# Revit family: Loudspeaker-Ceiling Mounted-Q-SYS-AD-C6T-High Ceiling
name_source: partatom
category: Communication Devices
units: mm (PartAtom-declared; Revit-internal decimal feet)

## family parameters
Cut with Voids When Loaded = No
Host = Face
Maintain Annotation Orientation = No
OmniClass Number = 23.85.10.11.14.14.14
OmniClass Title = Loudspeakers
Part Type = Normal
Room Calculation Point = No
Round Connector Dimension = Use Diameter
Shared = No

## types (1)
- White
    100V Taps = 15 W, 30 W, 60 W
    70V Taps = 7.5 W, 15 W, 30 W, 60 W
    ATB Inside Diameter = 12 "
    ATB Inside Radius = 6 "
    Assembly Code = E1020300
    Body Diameter = 11.4 "
    Body Height = 11.7 "
    Body Material = Paint - Q-SYS - Black
    Body Radius = 5.7 "
    Clip Diameter = 0.3 "
    Clip Height = 0.4 "
    Clip Radius = 0.15 "
    Cover Diameter = 11.5 "
    Cover Material = Paint - Q-SYS - White
    Cover Radius = 5.75 "
    Coverage Horizontal = 75.00°
    Coverage Vertical = 75.00°
    Default Elevation = 48 "
    Description = Ceiling-mount loudspeaker for high ceilings and/or reverberant spaces
    Frequency Range = 45 Hz - 20 kHz
    Grille Diameter = 13.4 "
    Grille Height = 0.2 "
    Grille Radius = 6.7 "
    Highlight Material = Fabric - Q-SYS - White Mesh
    IQ Category = Loudspeaker
    Impedance = 16
    Length 1 = 5.45 "
    Length 10 = 0.999 "
    Length 11 = 0.575 "
    Length 15 = 5.75 "
    Length 2 = 2.75 "
    Length 4 = 6.8 "
    Length 7 = 1 "
    Length 8 = 0.768 "
    Length 9 = 0.595 "
    Manufacturer = Q-SYS
    Manufacturer URL = https://www.qsys.com
    Model = AD-C6T
    Number of Bands = 1
    Offset = 0 "
    OmniClass Number = 23.85.10.11.14.14.14
    Part Number = AD-C6T
    Product Documentation Link = https://www.qsys.com
    Product Page URL = https://www.qsys.com
    Rail Width = 0.875 "
    Regulatory Compliance = CE
    SPL Max = 116
    Sensitivity = 90
    Support Length = 25.57 "
    Support Material = Metal - Q-SYS - Steel
    Support Width = 25.3 "
    Taper Angle = 3.00°
    Type Comments = Black DS 16F
    URL = https://www.qsys.com
    Unit Size = 16.2
    Weight = 19.00 lbm
    Weight Dimensional = 18.9
    Weight Product = 18.9
    Width = 13.4 "

## geometry (parser evidence)
native form markers: Blend x2, Sweep x5
no freeform markers — native parametric forms only
